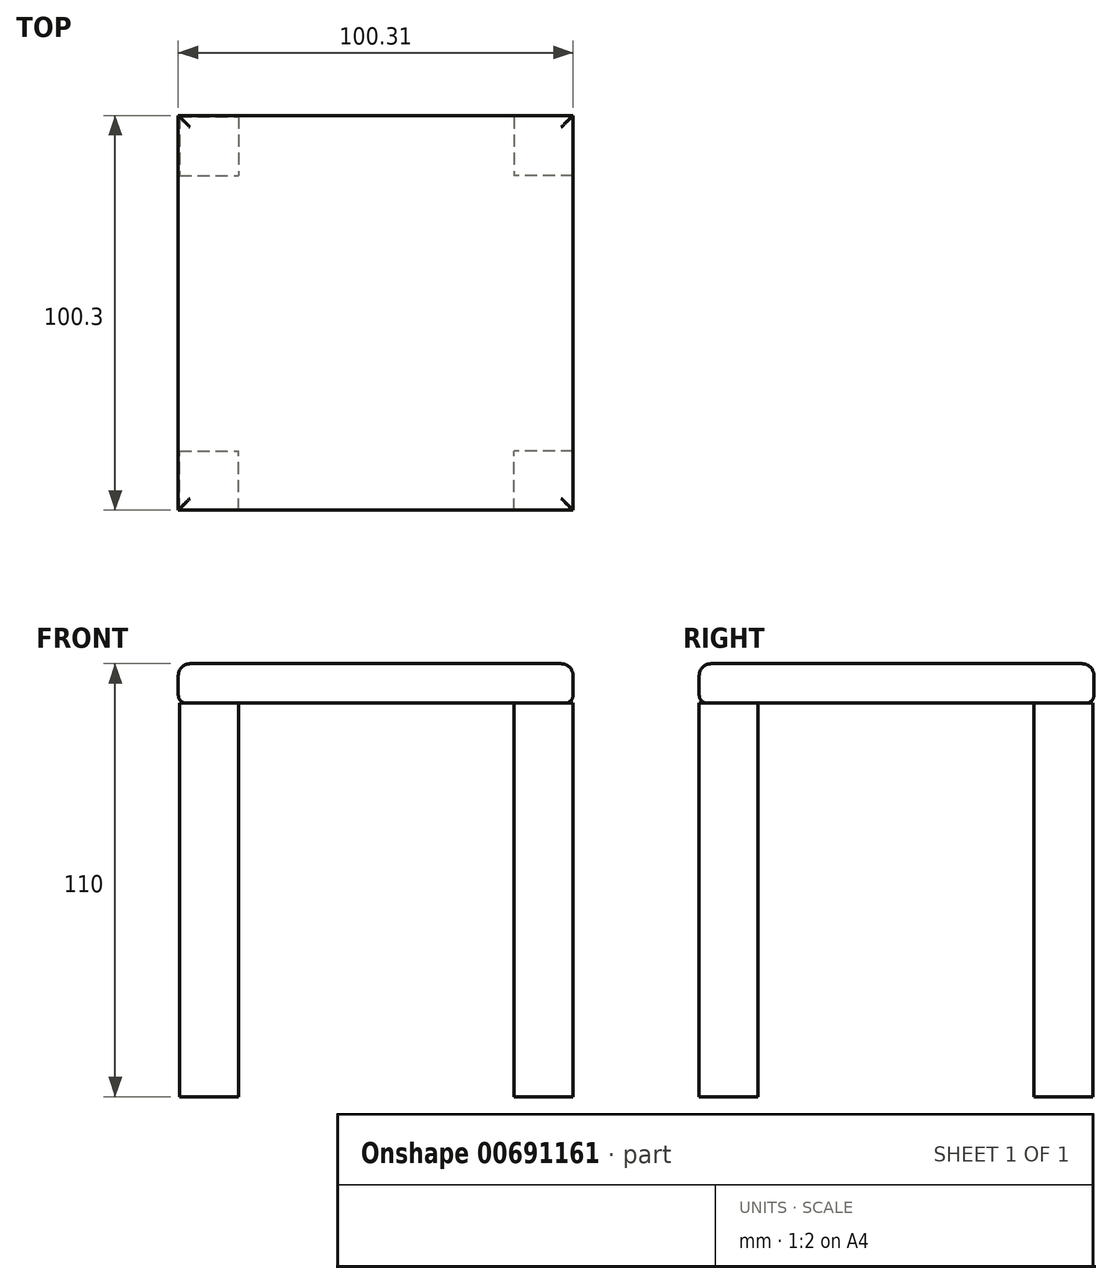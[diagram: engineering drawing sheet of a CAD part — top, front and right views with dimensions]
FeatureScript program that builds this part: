
annotation { "Feature Type Name" : "Feature", "Feature Type Description" : "" }
export const myFeature = defineFeature(function(context is Context, id is Id, definition is map)
    precondition{}
    {
        {
            var Q0;
            Q0=qCreatedBy(makeId("Top.planeOp"),FACE);
            var sketch = newSketch(context, id + "F0", { "sketchPlane" : qUnion([Q0])});
            skLineSegment(sketch, "E0.bottom", {"start": v(-85, 49.13) * mm, "end": v(-70, 49.13) * mm});
            skLineSegment(sketch, "E0.top", {"start": v(-85, -50.87) * mm, "end": v(-70, -50.87) * mm});
            skLineSegment(sketch, "E0.left", {"start": v(-85, 49.13) * mm, "end": v(-85, 34.13) * mm});
            skLineSegment(sketch, "E0.right", {"start": v(15, 49.13) * mm, "end": v(15, 34.13) * mm});
            skLineSegment(sketch, "E1.top", {"start": v(-85, 34.13) * mm, "end": v(-70, 34.13) * mm});
            skLineSegment(sketch, "E1.right", {"start": v(-70, 49.13) * mm, "end": v(-70, 34.13) * mm});
            skLineSegment(sketch, "E2.bottom", {"start": v(15, 49.13) * mm, "end": v(0, 49.13) * mm});
            skLineSegment(sketch, "E2.top", {"start": v(15, 34.13) * mm, "end": v(0, 34.13) * mm});
            skLineSegment(sketch, "E2.right", {"start": v(0, 49.13) * mm, "end": v(0, 34.13) * mm});
            skLineSegment(sketch, "E3.top", {"start": v(-85, -35.87) * mm, "end": v(-70, -35.87) * mm});
            skLineSegment(sketch, "E3.left", {"start": v(-85, -50.87) * mm, "end": v(-85, -35.87) * mm});
            skLineSegment(sketch, "E3.right", {"start": v(-70, -50.87) * mm, "end": v(-70, -35.87) * mm});
            skLineSegment(sketch, "E4.bottom", {"start": v(15, -50.87) * mm, "end": v(0, -50.87) * mm});
            skLineSegment(sketch, "E4.top", {"start": v(15, -35.87) * mm, "end": v(0, -35.87) * mm});
            skLineSegment(sketch, "E4.left", {"start": v(15, -50.87) * mm, "end": v(15, -35.87) * mm});
            skLineSegment(sketch, "E4.right", {"start": v(0, -50.87) * mm, "end": v(0, -35.87) * mm});
            skLineSegment(sketch, "E5.trimOffspring", {"start": v(0, 49.13) * mm, "end": v(15, 49.13) * mm});
            skLineSegment(sketch, "E6.trimOffspring", {"start": v(15, -35.87) * mm, "end": v(15, -50.87) * mm});
            skLineSegment(sketch, "E7.trimOffspring", {"start": v(-85, -35.87) * mm, "end": v(-85, -50.87) * mm});
            skLineSegment(sketch, "E8.trimOffspring", {"start": v(0, -50.87) * mm, "end": v(15, -50.87) * mm});
            skSolve(sketch);
        }
        {
            var Q0;
            Q0 = qSketchRegion(id + "F0", true);
            extrude(context, id + "F1", {"entities" : qUnion([Q0]), "depth" : -100 * mm, "offsetDistance" : 25 * mm});
        }
        {
            var Q0;
            Q0=qCreatedBy(makeId("Top.planeOp"),FACE);
            var sketch = newSketch(context, id + "F2", { "sketchPlane" : qUnion([Q0])});
            skLineSegment(sketch, "E9.bottom", {"start": v(-85.3, 49.43) * mm, "end": v(14.97, 49.43) * mm});
            skLineSegment(sketch, "E9.top", {"start": v(-85.3, -50.85) * mm, "end": v(14.97, -50.85) * mm});
            skLineSegment(sketch, "E9.left", {"start": v(-85.3, 49.43) * mm, "end": v(-85.3, -50.85) * mm});
            skLineSegment(sketch, "E9.right", {"start": v(14.97, 49.43) * mm, "end": v(14.97, -50.85) * mm});
            skSolve(sketch);
        }
        {
            var Q0;
            Q0=makeQuery(id+"F2.imprint","IMPRINT",FACE,{"disambiguationData":[TD([[makeQuery(id+"F2.imprint","IMPRINT",EDGE,{"derivedFrom":sQuery(id+"F2.wireOp",EDGE,"E9.bottom")}),-1.0]])]});
            extrude(context, id + "F3", {"entities" : qUnion([Q0]), "depth" : 10 * mm, "offsetDistance" : 25 * mm});
        }
        {
            var Q0;
            Q0=makeQuery(id+"F3.opExtrude","CAP_EDGE",EDGE,{"disambiguationData":[OSD([sQuery(id+"F2.wireOp",EDGE,"E9.left")])],"isStart":true});
            var Q1;
            Q1=makeQuery(id+"F3.opExtrude","CAP_FACE",FACE,{"disambiguationData":[OSD([sQuery(id+"F2.wireOp",EDGE,"E9.bottom"),sQuery(id+"F2.wireOp",EDGE,"E9.top"),sQuery(id+"F2.wireOp",EDGE,"E9.left"),sQuery(id+"F2.wireOp",EDGE,"E9.right")])],"isStart":true});
            var Q2;
            Q2=makeQuery(id+"F3.opExtrude","CAP_EDGE",EDGE,{"disambiguationData":[OSD([sQuery(id+"F2.wireOp",EDGE,"E9.bottom")])],"isStart":true});
            var Q3;
            Q3=makeQuery(id+"F3.opExtrude","CAP_EDGE",EDGE,{"disambiguationData":[OSD([sQuery(id+"F2.wireOp",EDGE,"E9.right")])],"isStart":true});
            var Q4;
            Q4=makeQuery(id+"F3.opExtrude","CAP_EDGE",EDGE,{"disambiguationData":[OSD([sQuery(id+"F2.wireOp",EDGE,"E9.top")])],"isStart":true});
            fillet(context, id + "F4", {"entities" : qUnion([Q0, Q1, Q2, Q3, Q4]), "radius" : 2 * mm, "tangentPropagation" : true, "allowEdgeOverflow" : false});
        }
        {
            var Q0;
            Q0=makeQuery(id+"F3.opExtrude","CAP_FACE",FACE,{"disambiguationData":[OSD([sQuery(id+"F2.wireOp",EDGE,"E9.bottom"),sQuery(id+"F2.wireOp",EDGE,"E9.top"),sQuery(id+"F2.wireOp",EDGE,"E9.left"),sQuery(id+"F2.wireOp",EDGE,"E9.right")])],"isStart":false});
            fillet(context, id + "F5", {"entities" : qUnion([Q0]), "radius" : 3 * mm, "tangentPropagation" : true, "allowEdgeOverflow" : false});
        }
    });
